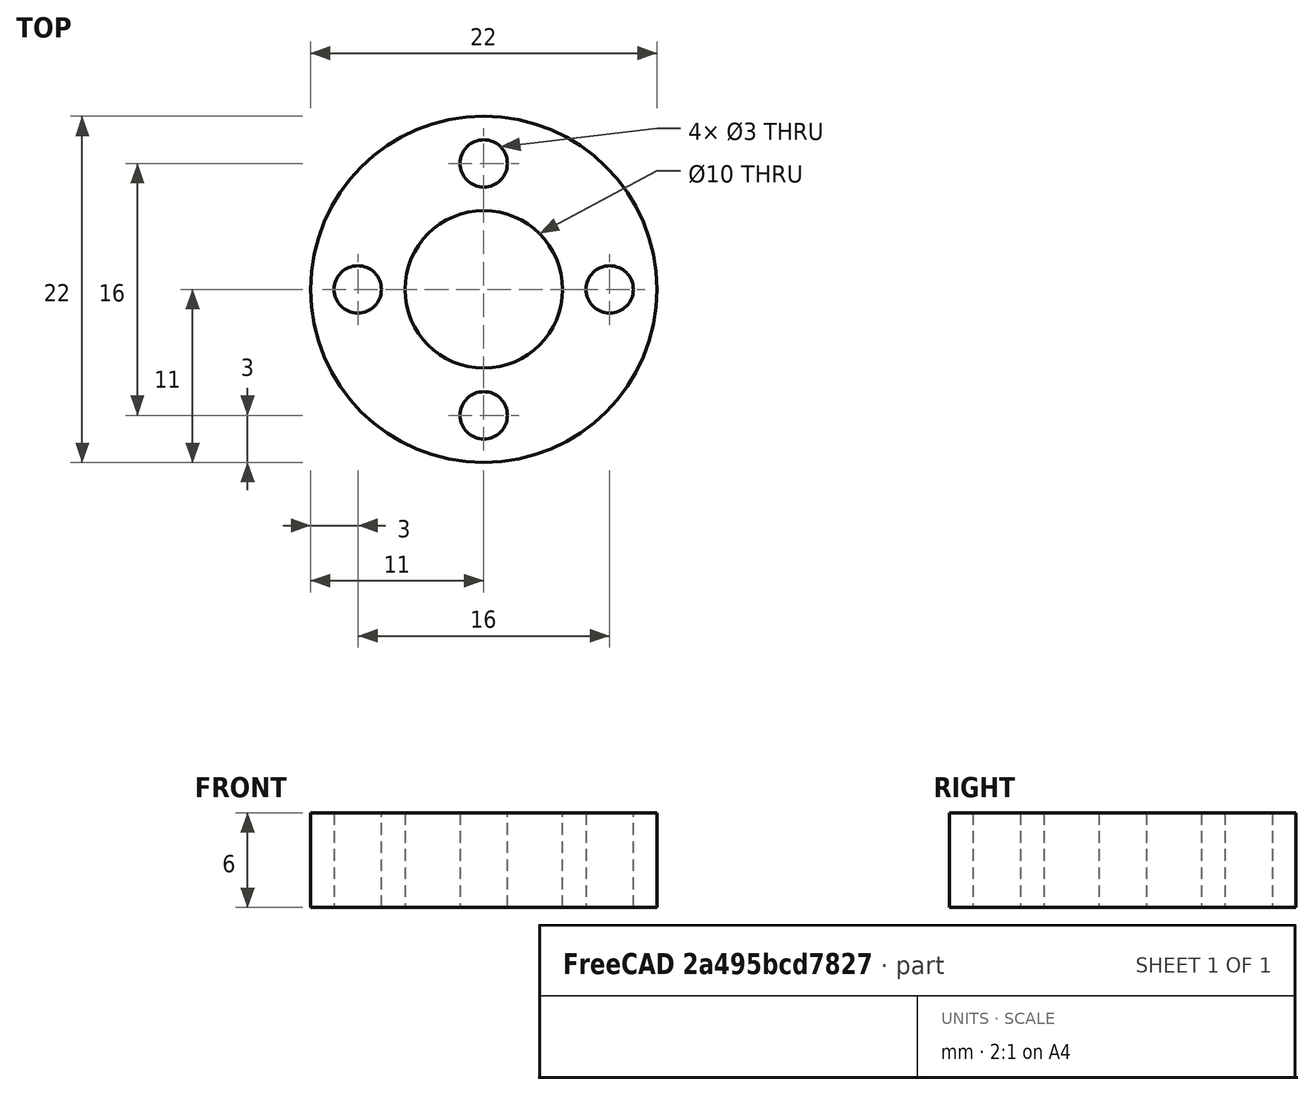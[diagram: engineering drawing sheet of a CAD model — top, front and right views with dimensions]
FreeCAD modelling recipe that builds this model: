
FCSTD DOCUMENT  (FreeCAD 0.19R)
Label: rondelle_assemblage_ecrous
License: All rights reserved
LicenseURL: http://en.wikipedia.org/wiki/All_rights_reserved
objects: Sketcher::SketchObject×1, PartDesign::Pad×1, PartDesign::Body×1
note: 4 computed .brp shape members not serialized (recipe doc carries the construction recipe); baked Part::Feature solids carry a one-line shape summary decoded from their .brp

FEATURE [Sketcher::SketchObject] Sketch
  FullyConstrained = true
  MapMode = 5
  Support = -> [XY_Plane]
  sketch-geometry (6):
    g0: Circle CenterX=0 CenterY=0 CenterZ=0 NormalX=0 NormalY=0 NormalZ=1 AngleXU=0 Radius=11
    g1: Circle CenterX=0 CenterY=8 CenterZ=0 NormalX=0 NormalY=0 NormalZ=1 AngleXU=0 Radius=1.5
    g2: Circle CenterX=-8 CenterY=0 CenterZ=0 NormalX=0 NormalY=0 NormalZ=1 AngleXU=0 Radius=1.5
    g3: Circle CenterX=0 CenterY=-8 CenterZ=0 NormalX=0 NormalY=0 NormalZ=1 AngleXU=0 Radius=1.5
    g4: Circle CenterX=8 CenterY=0 CenterZ=0 NormalX=0 NormalY=0 NormalZ=1 AngleXU=0 Radius=1.5
    g5: Circle CenterX=0 CenterY=0 CenterZ=0 NormalX=0 NormalY=0 NormalZ=1 AngleXU=0 Radius=5
  constraints (16):
    c: Coincident(g0,g-1)
    c: Radius(g0) = 11
    c: PointOnObject(g1,g-2)
    c: PointOnObject(g2,g-1)
    c: PointOnObject(g3,g-2)
    c: PointOnObject(g4,g-1)
    c: Radius(g1) = 1.5
    c: Radius(g2) = 1.5
    c: Radius(g3) = 1.5
    c: Radius(g4) = 1.5
    c: DistanceY(g0,g1) = 8
    c: DistanceY(g3,g0) = 8
    c: DistanceX(g2,g0) = 8
    c: DistanceX(g0,g4) = 8
    c: Coincident(g5,g0)
    c: Radius(g5) = 5
FEATURE [PartDesign::Pad] Pad
  Direction = (1,1,1)
  Length = 6
  Length2 = 100
  Profile = -> Sketch
  Type = 0
FEATURE [PartDesign::Body] Body
  Group = -> [Sketch,Pad]
  Origin = -> Origin
  Tip = -> Pad
